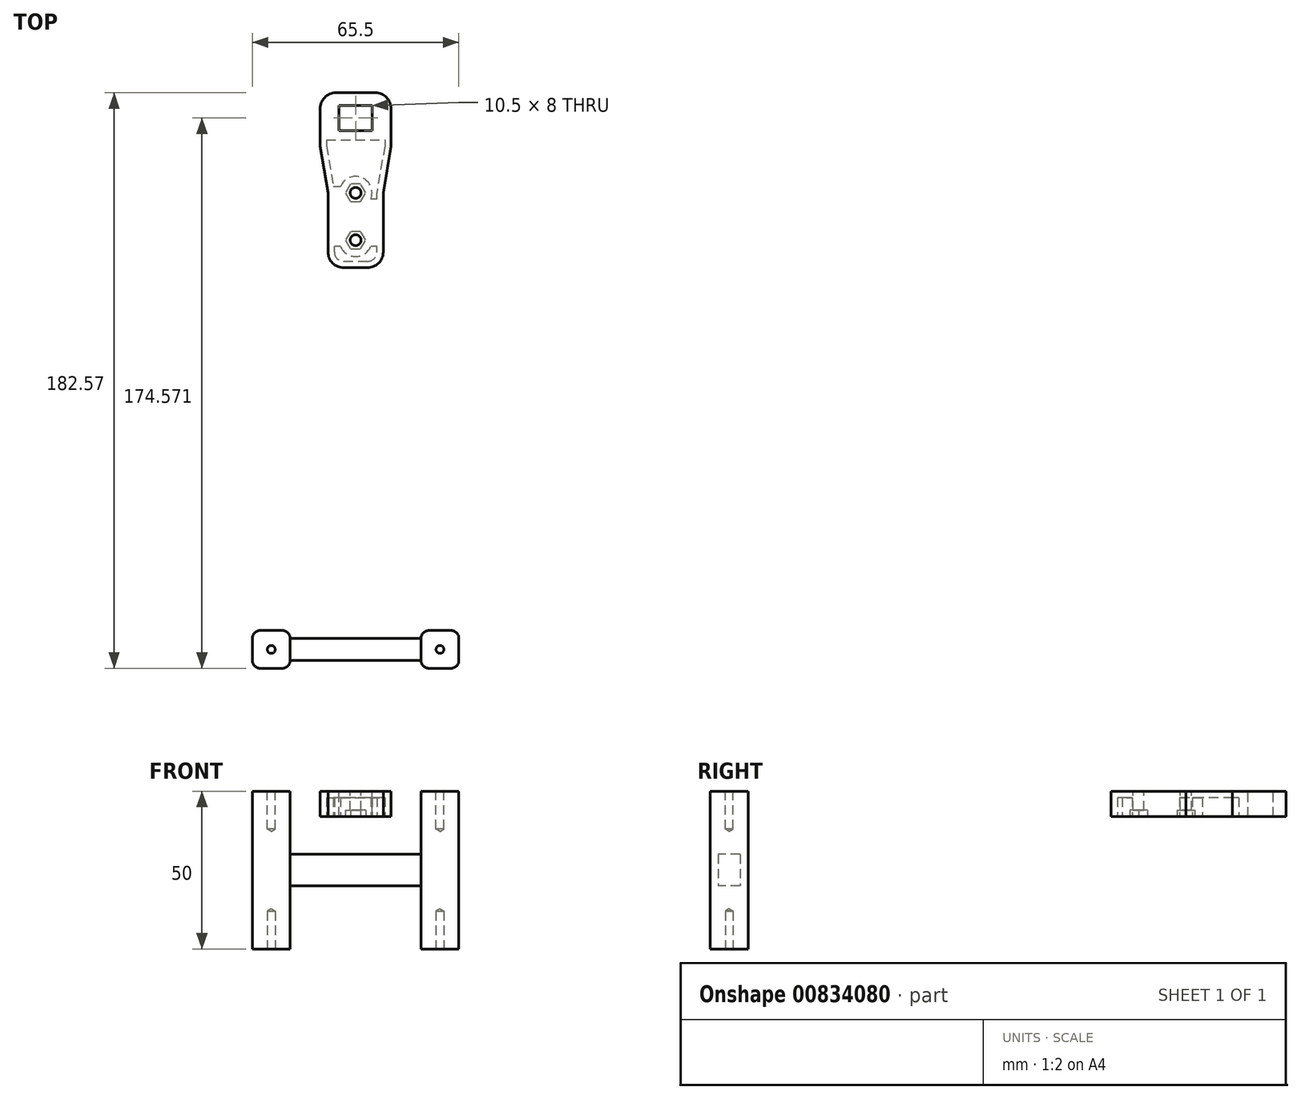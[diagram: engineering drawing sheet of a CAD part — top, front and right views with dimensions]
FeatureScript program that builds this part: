
annotation { "Feature Type Name" : "Feature", "Feature Type Description" : "" }
export const myFeature = defineFeature(function(context is Context, id is Id, definition is map)
    precondition{}
    {
        {
            var Q0;
            Q0=qCreatedBy(makeId("Top.planeOp"),FACE);
            cPlane(context, id + "F0", {"entities" : qUnion([Q0]), "cplaneType" : CPlaneType.OFFSET, "offset" : 5 * mm, "oppositeDirection" : true, "width" : 150 * mm, "height" : 150 * mm});
        }
        {
            var Q0;
            Q0=qCreatedBy(makeId("Top.planeOp"),FACE);
            cPlane(context, id + "F1", {"entities" : qUnion([Q0]), "cplaneType" : CPlaneType.OFFSET, "offset" : 50 * mm, "oppositeDirection" : true, "width" : 150 * mm, "height" : 150 * mm});
        }
        {
            var Q0;
            Q0=qCreatedBy(id+"F1.planeOp",FACE);
            cPlane(context, id + "F2", {"entities" : qUnion([Q0]), "cplaneType" : CPlaneType.OFFSET, "offset" : 5 * mm, "width" : 150 * mm, "height" : 150 * mm});
        }
        {
            var Q0;
            Q0=qCreatedBy(id+"F0.planeOp",FACE);
            var sketch = newSketch(context, id + "F3", { "sketchPlane" : qUnion([Q0])});
            skLineSegment(sketch, "E0.bottom", {"start": v(28, -42.5) * mm, "end": v(-28, -42.5) * mm});
            skLineSegment(sketch, "E0.top", {"start": v(28, 42.5) * mm, "end": v(-28, 42.5) * mm});
            skLineSegment(sketch, "E0.left", {"start": v(28, -42.5) * mm, "end": v(28, 42.5) * mm});
            skLineSegment(sketch, "E0.right", {"start": v(-28, -42.5) * mm, "end": v(-28, 42.5) * mm});
            skPoint(sketch, "E0.middle", {"position": v(0, 0) * mm});
            skLineSegment(sketch, "E1", {"start": v(0, 42.5) * mm, "end": v(0, -42.5) * mm, "construction": true});
            skLineSegment(sketch, "E2.bottom", {"start": v(-24.5, 19) * mm, "end": v(24.5, 19) * mm, "construction": true});
            skLineSegment(sketch, "E2.top", {"start": v(-24.5, -39) * mm, "end": v(24.5, -39) * mm, "construction": true});
            skLineSegment(sketch, "E2.left", {"start": v(-24.5, 19) * mm, "end": v(-24.5, -39) * mm, "construction": true});
            skLineSegment(sketch, "E2.right", {"start": v(24.5, 19) * mm, "end": v(24.5, -39) * mm, "construction": true});
            skPoint(sketch, "E3", {"position": v(0, -39) * mm});
            skCircle(sketch, "E4", {"center": v(-24.5, 19) * mm, "radius": 1.38 * mm});
            skCircle(sketch, "E5", {"center": v(24.5, 19) * mm, "radius": 1.38 * mm});
            skCircle(sketch, "E6", {"center": v(-24.5, -39) * mm, "radius": 1.38 * mm});
            skCircle(sketch, "E7", {"center": v(24.5, -39) * mm, "radius": 1.38 * mm});
            skSolve(sketch);
        }
        {
            var Q0;
            Q0=qCreatedBy(id+"F2.planeOp",FACE);
            var sketch = newSketch(context, id + "F4", { "sketchPlane" : qUnion([Q0])});
            skLineSegment(sketch, "E8.bottom", {"start": v(26.65, -50.8) * mm, "end": v(-26.65, -50.8) * mm});
            skLineSegment(sketch, "E8.top", {"start": v(26.65, 50.8) * mm, "end": v(-26.65, 50.8) * mm});
            skLineSegment(sketch, "E8.left", {"start": v(26.65, -50.8) * mm, "end": v(26.65, 50.8) * mm});
            skLineSegment(sketch, "E8.right", {"start": v(-26.65, -50.8) * mm, "end": v(-26.65, 50.8) * mm});
            skPoint(sketch, "E8.middle", {"position": v(0, 0) * mm});
            skLineSegment(sketch, "E9", {"start": v(-24.15, 36.8) * mm, "end": v(-24.15, -45.4) * mm, "construction": true});
            skCircle(sketch, "E10", {"center": v(-24.15, 36.8) * mm, "radius": 1.75 * mm});
            skLineSegment(sketch, "E11", {"start": v(24.05, 35.5) * mm, "end": v(24.05, -39.4) * mm, "construction": true});
            skLineSegment(sketch, "E12", {"start": v(-19.05, -15.3) * mm, "end": v(8.85, -15.3) * mm, "construction": true});
            skCircle(sketch, "E13", {"center": v(-24.15, -45.4) * mm, "radius": 1.75 * mm});
            skCircle(sketch, "E14", {"center": v(-19.05, -15.3) * mm, "radius": 1.75 * mm});
            skCircle(sketch, "E15", {"center": v(8.85, -15.3) * mm, "radius": 1.75 * mm});
            skCircle(sketch, "E16", {"center": v(24.05, -39.4) * mm, "radius": 1.75 * mm});
            skCircle(sketch, "E17", {"center": v(24.05, 35.5) * mm, "radius": 1.75 * mm});
            skSolve(sketch);
        }
        {
            var Q0;
            Q0=qCreatedBy(makeId("Top.planeOp"),FACE);
            var sketch = newSketch(context, id + "F5", { "sketchPlane" : qUnion([Q0])});
            skPoint(sketch, "E18", {"position": v(-78, 0) * mm});
            skLineSegment(sketch, "E19", {"start": v(-78, 0) * mm, "end": v(0, 0) * mm, "construction": true});
            skPoint(sketch, "E20", {"position": v(-35, 0) * mm});
            skArc(sketch, "E21", {"start": v(-41.72, 93.39) * mm, "mid": v(-69.28, 91.47) * mm, "end": v(-68.64, 63.86) * mm});
            skArc(sketch, "E22", {"start": v(-81.47, 19.7) * mm, "mid": v(-98, 0) * mm, "end": v(-81.47, -19.7) * mm});
            skLineSegment(sketch, "E23", {"start": v(-54.5, 78) * mm, "end": v(0, 78) * mm, "construction": true});
            skLineSegment(sketch, "E24", {"start": v(0, 78) * mm, "end": v(0, 0) * mm, "construction": true});
            skArc(sketch, "E25.MirrorC", {"start": v(-41.72, -93.39) * mm, "mid": v(-69.28, -91.47) * mm, "end": v(-68.64, -63.86) * mm});
            skArc(sketch, "E26.MirrorC", {"start": v(41.72, 93.39) * mm, "mid": v(69.28, 91.47) * mm, "end": v(68.64, 63.86) * mm});
            skArc(sketch, "E27.MirrorC", {"start": v(81.47, 19.7) * mm, "mid": v(98, 0) * mm, "end": v(81.47, -19.7) * mm});
            skArc(sketch, "E28.MirrorC", {"start": v(41.72, -93.39) * mm, "mid": v(69.28, -91.47) * mm, "end": v(68.64, -63.86) * mm});
            skLineSegment(sketch, "E29", {"start": v(-54.5, 78) * mm, "end": v(-84.27, 48.23) * mm, "construction": true});
            skLineSegment(sketch, "E30", {"start": v(-78, 0) * mm, "end": v(-85.72, 43.8) * mm, "construction": true});
            skArc(sketch, "E31", {"start": v(-81.47, 19.7) * mm, "mid": v(-62.72, 38.2) * mm, "end": v(-68.64, 63.86) * mm});
            skArc(sketch, "E32.MirrorCS", {"start": v(-81.47, -19.7) * mm, "mid": v(-62.72, -38.2) * mm, "end": v(-68.64, -63.86) * mm});
            skArc(sketch, "E33.MirrorCS", {"start": v(81.47, 19.7) * mm, "mid": v(62.72, 38.2) * mm, "end": v(68.64, 63.86) * mm});
            skArc(sketch, "E34.MirrorCS", {"start": v(81.47, -19.7) * mm, "mid": v(62.72, -38.2) * mm, "end": v(68.64, -63.86) * mm});
            skPoint(sketch, "E35", {"position": v(0, 143.63) * mm});
            skLineSegment(sketch, "E36", {"start": v(54.5, 78) * mm, "end": v(0, 143.63) * mm, "construction": true});
            skArc(sketch, "E37", {"start": v(41.72, 93.39) * mm, "mid": v(0, 78.32) * mm, "end": v(-41.72, 93.39) * mm});
            skArc(sketch, "E38.MirrorCS", {"start": v(41.72, -93.39) * mm, "mid": v(0, -78.32) * mm, "end": v(-41.72, -93.39) * mm});
            skLineSegment(sketch, "E39", {"start": v(-65, 78) * mm, "end": v(-44, 78) * mm, "construction": true});
            skLineSegment(sketch, "E40", {"start": v(-54.5, 88.5) * mm, "end": v(-54.5, 67.5) * mm, "construction": true});
            skCircle(sketch, "E41", {"center": v(-54.5, 88.5) * mm, "radius": 1.25 * mm});
            skCircle(sketch, "E42", {"center": v(-44, 78) * mm, "radius": 1.25 * mm});
            skCircle(sketch, "E43", {"center": v(-54.5, 67.5) * mm, "radius": 1.25 * mm});
            skCircle(sketch, "E44", {"center": v(-65, 78) * mm, "radius": 1.25 * mm});
            skCircle(sketch, "E45", {"center": v(-54.5, 78) * mm, "radius": 4.5 * mm});
            skCircle(sketch, "E46.MirrorC", {"center": v(-54.5, -88.5) * mm, "radius": 1.25 * mm});
            skCircle(sketch, "E47.MirrorC", {"center": v(-44, -78) * mm, "radius": 1.25 * mm});
            skCircle(sketch, "E48.MirrorC", {"center": v(-54.5, -67.5) * mm, "radius": 1.25 * mm});
            skCircle(sketch, "E49.MirrorC", {"center": v(-65, -78) * mm, "radius": 1.25 * mm});
            skCircle(sketch, "E50.MirrorC", {"center": v(-54.5, -78) * mm, "radius": 4.5 * mm});
            skCircle(sketch, "E51.MirrorC", {"center": v(54.5, 88.5) * mm, "radius": 1.25 * mm});
            skCircle(sketch, "E52.MirrorC", {"center": v(44, 78) * mm, "radius": 1.25 * mm});
            skCircle(sketch, "E53.MirrorC", {"center": v(54.5, 67.5) * mm, "radius": 1.25 * mm});
            skCircle(sketch, "E54.MirrorC", {"center": v(65, 78) * mm, "radius": 1.25 * mm});
            skCircle(sketch, "E55.MirrorC", {"center": v(54.5, 78) * mm, "radius": 4.5 * mm});
            skCircle(sketch, "E56.MirrorC", {"center": v(54.5, -67.5) * mm, "radius": 1.25 * mm});
            skCircle(sketch, "E57.MirrorC", {"center": v(44, -78) * mm, "radius": 1.25 * mm});
            skCircle(sketch, "E58.MirrorC", {"center": v(54.5, -88.5) * mm, "radius": 1.25 * mm});
            skCircle(sketch, "E59.MirrorC", {"center": v(65, -78) * mm, "radius": 1.25 * mm});
            skCircle(sketch, "E60.MirrorC", {"center": v(54.5, -78) * mm, "radius": 4.5 * mm});
            skLineSegment(sketch, "E61", {"start": v(-88.5, 0) * mm, "end": v(-67.5, 0) * mm, "construction": true});
            skLineSegment(sketch, "E62", {"start": v(-78, 10.5) * mm, "end": v(-78, -10.5) * mm, "construction": true});
            skCircle(sketch, "E63", {"center": v(-78, 10.5) * mm, "radius": 1.25 * mm});
            skCircle(sketch, "E64", {"center": v(-67.5, 0) * mm, "radius": 1.25 * mm});
            skCircle(sketch, "E65", {"center": v(-78, -10.5) * mm, "radius": 1.25 * mm});
            skCircle(sketch, "E66", {"center": v(-88.5, 0) * mm, "radius": 1.25 * mm});
            skCircle(sketch, "E67", {"center": v(-78, 0) * mm, "radius": 4.5 * mm});
            skCircle(sketch, "E68.MirrorC", {"center": v(78, 0) * mm, "radius": 4.5 * mm});
            skCircle(sketch, "E69.MirrorC", {"center": v(67.5, 0) * mm, "radius": 1.25 * mm});
            skCircle(sketch, "E70.MirrorC", {"center": v(78, 10.5) * mm, "radius": 1.25 * mm});
            skCircle(sketch, "E71.MirrorC", {"center": v(88.5, 0) * mm, "radius": 1.25 * mm});
            skCircle(sketch, "E72.MirrorC", {"center": v(78, -10.5) * mm, "radius": 1.25 * mm});
            skCircle(sketch, "E73", {"center": v(-26.75, 74.5) * mm, "radius": 1.75 * mm});
            skCircle(sketch, "E74.MirrorC", {"center": v(26.75, 74.5) * mm, "radius": 1.75 * mm});
            skCircle(sketch, "E75.MirrorC", {"center": v(-26.75, -74.5) * mm, "radius": 1.75 * mm});
            skCircle(sketch, "E76.MirrorC", {"center": v(26.75, -74.5) * mm, "radius": 1.75 * mm});
            skCircle(sketch, "E77", {"center": v(0, 70.32) * mm, "radius": 1.75 * mm});
            skCircle(sketch, "E78", {"center": v(0, 55.32) * mm, "radius": 1.75 * mm});
            skLineSegment(sketch, "E79.bottom", {"start": v(-21, 12.5) * mm, "end": v(-17, 12.5) * mm});
            skLineSegment(sketch, "E79.top", {"start": v(-21, -12.5) * mm, "end": v(-17, -12.5) * mm});
            skLineSegment(sketch, "E79.left", {"start": v(-21, 12.5) * mm, "end": v(-21, -12.5) * mm});
            skLineSegment(sketch, "E79.right", {"start": v(-17, 12.5) * mm, "end": v(-17, -12.5) * mm});
            skPoint(sketch, "E80", {"position": v(-17, 0) * mm});
            skLineSegment(sketch, "E81.MirrorCS", {"start": v(17, 12.5) * mm, "end": v(17, -12.5) * mm});
            skLineSegment(sketch, "E82.MirrorCS", {"start": v(21, 12.5) * mm, "end": v(21, -12.5) * mm});
            skLineSegment(sketch, "E83.MirrorCS", {"start": v(21, -12.5) * mm, "end": v(17, -12.5) * mm});
            skLineSegment(sketch, "E84.MirrorCS", {"start": v(21, 12.5) * mm, "end": v(17, 12.5) * mm});
            skCircle(sketch, "E85.0", {"center": v(24.5, 19) * mm, "radius": 1.38 * mm});
            skCircle(sketch, "E86.0", {"center": v(24.5, -39) * mm, "radius": 1.38 * mm});
            skCircle(sketch, "E87.0", {"center": v(-24.5, -39) * mm, "radius": 1.38 * mm});
            skCircle(sketch, "E88.0", {"center": v(-24.5, 19) * mm, "radius": 1.38 * mm});
            skLineSegment(sketch, "E89", {"start": v(-26.75, -74.5) * mm, "end": v(26.75, -74.5) * mm, "construction": true});
            skSolve(sketch);
        }
        {
            var Q0;
            Q0=qCreatedBy(id+"F1.planeOp",FACE);
            var sketch = newSketch(context, id + "F6", { "sketchPlane" : qUnion([Q0])});
            skArc(sketch, "E90.0", {"start": v(41.72, 93.39) * mm, "mid": v(0, 78.32) * mm, "end": v(-41.72, 93.39) * mm});
            skArc(sketch, "E91.0", {"start": v(-41.72, 93.39) * mm, "mid": v(-69.28, 91.47) * mm, "end": v(-68.64, 63.86) * mm});
            skArc(sketch, "E92.0", {"start": v(-81.47, 19.7) * mm, "mid": v(-62.72, 38.2) * mm, "end": v(-68.64, 63.86) * mm});
            skArc(sketch, "E93.0", {"start": v(-81.47, 19.7) * mm, "mid": v(-98, 0) * mm, "end": v(-81.47, -19.7) * mm});
            skArc(sketch, "E94.0", {"start": v(-81.47, -19.7) * mm, "mid": v(-62.72, -38.2) * mm, "end": v(-68.64, -63.86) * mm});
            skArc(sketch, "E95.0", {"start": v(-41.72, -93.39) * mm, "mid": v(-69.28, -91.47) * mm, "end": v(-68.64, -63.86) * mm});
            skArc(sketch, "E96.0", {"start": v(41.72, -93.39) * mm, "mid": v(0, -78.32) * mm, "end": v(-41.72, -93.39) * mm});
            skArc(sketch, "E97.0", {"start": v(41.72, -93.39) * mm, "mid": v(69.28, -91.47) * mm, "end": v(68.64, -63.86) * mm});
            skArc(sketch, "E98.0", {"start": v(81.47, -19.7) * mm, "mid": v(62.72, -38.2) * mm, "end": v(68.64, -63.86) * mm});
            skArc(sketch, "E99.0", {"start": v(81.47, 19.7) * mm, "mid": v(98, 0) * mm, "end": v(81.47, -19.7) * mm});
            skArc(sketch, "E100.0", {"start": v(81.47, 19.7) * mm, "mid": v(62.72, 38.2) * mm, "end": v(68.64, 63.86) * mm});
            skArc(sketch, "E101.0", {"start": v(41.72, 93.39) * mm, "mid": v(69.28, 91.47) * mm, "end": v(68.64, 63.86) * mm});
            skCircle(sketch, "E102.0", {"center": v(26.75, 74.5) * mm, "radius": 1.75 * mm});
            skCircle(sketch, "E103.0", {"center": v(-26.75, 74.5) * mm, "radius": 1.75 * mm});
            skCircle(sketch, "E104.0", {"center": v(26.75, -74.5) * mm, "radius": 1.75 * mm});
            skCircle(sketch, "E105.0", {"center": v(-26.75, -74.5) * mm, "radius": 1.75 * mm});
            skCircle(sketch, "E106", {"center": v(-78, 0) * mm, "radius": 2.25 * mm});
            skCircle(sketch, "E107", {"center": v(-54.5, 78) * mm, "radius": 2.25 * mm});
            skLineSegment(sketch, "E108.0", {"start": v(0, 78) * mm, "end": v(0, 0) * mm, "construction": true});
            skLineSegment(sketch, "E109.0", {"start": v(-78, 0) * mm, "end": v(0, 0) * mm, "construction": true});
            skCircle(sketch, "E110.MirrorC", {"center": v(-54.5, -78) * mm, "radius": 2.25 * mm});
            skCircle(sketch, "E111.MirrorC", {"center": v(54.5, 78) * mm, "radius": 2.25 * mm});
            skCircle(sketch, "E112.MirrorC", {"center": v(78, 0) * mm, "radius": 2.25 * mm});
            skCircle(sketch, "E113.MirrorC", {"center": v(54.5, -78) * mm, "radius": 2.25 * mm});
            skCircle(sketch, "E114.0", {"center": v(-24.15, 36.8) * mm, "radius": 1.75 * mm});
            skCircle(sketch, "E115.0", {"center": v(-19.05, -15.3) * mm, "radius": 1.75 * mm});
            skCircle(sketch, "E116.0", {"center": v(-24.15, -45.4) * mm, "radius": 1.75 * mm});
            skCircle(sketch, "E117.0", {"center": v(24.05, -39.4) * mm, "radius": 1.75 * mm});
            skCircle(sketch, "E118.0", {"center": v(8.85, -15.3) * mm, "radius": 1.75 * mm});
            skCircle(sketch, "E119.0", {"center": v(24.05, 35.5) * mm, "radius": 1.75 * mm});
            skSolve(sketch);
        }
        {
            var Q0;
            Q0=qCreatedBy(makeId("Top.planeOp"),FACE);
            var sketch = newSketch(context, id + "F7", { "sketchPlane" : qUnion([Q0])});
            skCircle(sketch, "E120.0", {"center": v(0, 70.32) * mm, "radius": 1.75 * mm});
            skCircle(sketch, "E121.0", {"center": v(0, 55.32) * mm, "radius": 1.75 * mm});
            skLineSegment(sketch, "E122", {"start": v(0, 0) * mm, "end": v(0, 115.27) * mm, "construction": true});
            skLineSegment(sketch, "E123.bottom", {"start": v(8.75, 46.57) * mm, "end": v(-8.75, 46.57) * mm});
            skLineSegment(sketch, "E123.top", {"start": v(8.75, 102.07) * mm, "end": v(-8.75, 102.07) * mm});
            skLineSegment(sketch, "E123.left", {"start": v(8.75, 46.57) * mm, "end": v(8.75, 102.07) * mm});
            skLineSegment(sketch, "E123.right", {"start": v(-8.75, 46.57) * mm, "end": v(-8.75, 102.07) * mm});
            skPoint(sketch, "E123.middle", {"position": v(0, 74.32) * mm});
            skLineSegment(sketch, "E124.bottom", {"start": v(5.25, 90.07) * mm, "end": v(-5.25, 90.07) * mm});
            skLineSegment(sketch, "E124.top", {"start": v(5.25, 98.07) * mm, "end": v(-5.25, 98.07) * mm});
            skLineSegment(sketch, "E124.left", {"start": v(5.25, 90.07) * mm, "end": v(5.25, 98.07) * mm});
            skLineSegment(sketch, "E124.right", {"start": v(-5.25, 90.07) * mm, "end": v(-5.25, 98.07) * mm});
            skPoint(sketch, "E124.middle", {"position": v(0, 94.07) * mm});
            skLineSegment(sketch, "E125.bottom", {"start": v(-11.25, 102.07) * mm, "end": v(11.25, 102.07) * mm});
            skLineSegment(sketch, "E125.top", {"start": v(-11.25, 85.07) * mm, "end": v(11.25, 85.07) * mm});
            skLineSegment(sketch, "E125.left", {"start": v(-11.25, 102.07) * mm, "end": v(-11.25, 85.07) * mm});
            skLineSegment(sketch, "E125.right", {"start": v(11.25, 102.07) * mm, "end": v(11.25, 85.07) * mm});
            skPoint(sketch, "E125.middle", {"position": v(0, 93.57) * mm});
            skLineSegment(sketch, "E126", {"start": v(11.25, 85.07) * mm, "end": v(8.75, 70.32) * mm});
            skLineSegment(sketch, "E127", {"start": v(-11.25, 85.07) * mm, "end": v(-8.75, 70.32) * mm});
            skSolve(sketch);
        }
        {
            var Q0;
            {var subQ5=sQuery(id+"F7.wireOp",EDGE,"E125.right");Q0=makeQuery(id+"F7.imprint","IMPRINT",FACE,{"disambiguationData":[TD([[makeQuery(id+"F7.imprint","IMPRINT",EDGE,{"derivedFrom":subQ5}),-1.0]])]});}
            var Q1;
            Q1=makeQuery(id+"F7.imprint","IMPRINT",FACE,{"disambiguationData":[TD([[makeQuery(id+"F7.imprint","IMPRINT",EDGE,{"derivedFrom":sQuery(id+"F7.wireOp",EDGE,"E124.bottom")}),1.0]])]});
            var Q2;
            {var subQ5=sQuery(id+"F7.wireOp",EDGE,"E125.left");Q2=makeQuery(id+"F7.imprint","IMPRINT",FACE,{"disambiguationData":[TD([[makeQuery(id+"F7.imprint","IMPRINT",EDGE,{"derivedFrom":subQ5}),1.0]])]});}
            var Q3;
            {var subQ0=sQuery(id+"F7.wireOp",EDGE,"E127");Q3=makeQuery(id+"F7.imprint","IMPRINT",FACE,{"disambiguationData":[TD([[makeQuery(id+"F7.imprint","IMPRINT",EDGE,{"derivedFrom":subQ0}),1.0]])]});}
            var Q4;
            Q4=makeQuery(id+"F7.imprint","IMPRINT",FACE,{"disambiguationData":[TD([[makeQuery(id+"F7.imprint","IMPRINT",EDGE,{"derivedFrom":sQuery(id+"F7.wireOp",EDGE,"E120.0")}),-1.0]])]});
            var Q5;
            {var subQ0=sQuery(id+"F7.wireOp",EDGE,"E126");Q5=makeQuery(id+"F7.imprint","IMPRINT",FACE,{"disambiguationData":[TD([[makeQuery(id+"F7.imprint","IMPRINT",EDGE,{"derivedFrom":subQ0}),-1.0]])]});}
            extrude(context, id + "F8", {"entities" : qUnion([Q0, Q1, Q2, Q3, Q4, Q5]), "oppositeDirection" : true, "depth" : 8 * mm});
        }
        {
            var Q0;
            Q0=makeQuery(id+"F8.opExtrude","SWEPT_EDGE",EDGE,{"disambiguationData":[OSD([sQuery(id+"F7.wireOp",EDGE,"E125.bottom"),sQuery(id+"F7.wireOp",EDGE,"E125.right")])]});
            var Q1;
            Q1=makeQuery(id+"F8.opExtrude","SWEPT_EDGE",EDGE,{"disambiguationData":[OSD([sQuery(id+"F7.wireOp",EDGE,"E123.bottom"),sQuery(id+"F7.wireOp",EDGE,"E123.left")])]});
            var Q2;
            Q2=makeQuery(id+"F8.opExtrude","SWEPT_EDGE",EDGE,{"disambiguationData":[OSD([sQuery(id+"F7.wireOp",EDGE,"E123.bottom"),sQuery(id+"F7.wireOp",EDGE,"E123.right")])]});
            var Q3;
            Q3=makeQuery(id+"F8.opExtrude","SWEPT_EDGE",EDGE,{"disambiguationData":[OSD([sQuery(id+"F7.wireOp",EDGE,"E125.bottom"),sQuery(id+"F7.wireOp",EDGE,"E125.left")])]});
            fillet(context, id + "F9", {"entities" : qUnion([Q0, Q1, Q2, Q3]), "radius" : 5 * mm, "tangentPropagation" : true, "allowEdgeOverflow" : false});
        }
        {
            var Q0;
            Q0=makeQuery(id+"F8.opExtrude","CAP_FACE",FACE,{"disambiguationData":[OSD([sQuery(id+"F7.wireOp",EDGE,"E120.0"),sQuery(id+"F7.wireOp",EDGE,"E121.0"),sQuery(id+"F7.wireOp",EDGE,"E123.bottom"),sQuery(id+"F7.wireOp",EDGE,"E123.left"),sQuery(id+"F7.wireOp",EDGE,"E123.right"),sQuery(id+"F7.wireOp",EDGE,"E124.bottom"),sQuery(id+"F7.wireOp",EDGE,"E124.top"),sQuery(id+"F7.wireOp",EDGE,"E124.left"),sQuery(id+"F7.wireOp",EDGE,"E124.right"),sQuery(id+"F7.wireOp",EDGE,"E125.bottom"),sQuery(id+"F7.wireOp",EDGE,"E125.left"),sQuery(id+"F7.wireOp",EDGE,"E125.right"),sQuery(id+"F7.wireOp",EDGE,"E126"),sQuery(id+"F7.wireOp",EDGE,"E127")])],"isStart":false});
            var sketch = newSketch(context, id + "F10", { "sketchPlane" : qUnion([Q0])});
            skCircle(sketch, "E128.cCircle", {"center": v(0, -55.32) * mm, "radius": 2.77 * mm, "construction": true});
            skLineSegment(sketch, "E128.0", {"start": v(1.6, -58.1) * mm, "end": v(-1.6, -58.1) * mm});
            skLineSegment(sketch, "E128.1", {"start": v(-1.6, -58.1) * mm, "end": v(-3.2, -55.32) * mm});
            skLineSegment(sketch, "E128.2", {"start": v(-3.2, -55.32) * mm, "end": v(-1.6, -52.55) * mm});
            skLineSegment(sketch, "E128.3", {"start": v(-1.6, -52.55) * mm, "end": v(1.6, -52.55) * mm});
            skLineSegment(sketch, "E128.4", {"start": v(1.6, -52.55) * mm, "end": v(3.2, -55.32) * mm});
            skLineSegment(sketch, "E128.5", {"start": v(3.2, -55.32) * mm, "end": v(1.6, -58.1) * mm});
            skPoint(sketch, "E128.0.midPoint", {"position": v(0, -58.1) * mm});
            skCircle(sketch, "E129.cCircle", {"center": v(0, -70.32) * mm, "radius": 2.77 * mm, "construction": true});
            skLineSegment(sketch, "E129.0", {"start": v(-1.6, -67.55) * mm, "end": v(1.6, -67.55) * mm});
            skLineSegment(sketch, "E129.1", {"start": v(1.6, -67.55) * mm, "end": v(3.2, -70.32) * mm});
            skLineSegment(sketch, "E129.2", {"start": v(3.2, -70.32) * mm, "end": v(1.6, -73.1) * mm});
            skLineSegment(sketch, "E129.3", {"start": v(1.6, -73.1) * mm, "end": v(-1.6, -73.1) * mm});
            skLineSegment(sketch, "E129.4", {"start": v(-1.6, -73.1) * mm, "end": v(-3.2, -70.32) * mm});
            skLineSegment(sketch, "E129.5", {"start": v(-3.2, -70.32) * mm, "end": v(-1.6, -67.55) * mm});
            skPoint(sketch, "E129.0.midPoint", {"position": v(0, -67.55) * mm});
            skLineSegment(sketch, "E130.0", {"start": v(-9.25, -87.07) * mm, "end": v(-9.25, -85.24) * mm});
            skLineSegment(sketch, "E130.1", {"start": v(-9.25, -85.24) * mm, "end": v(-6.75, -70.49) * mm});
            skLineSegment(sketch, "E130.2", {"start": v(-6.75, -51.57) * mm, "end": v(-6.75, -70.49) * mm});
            skArc(sketch, "E130.3", {"start": v(-3.75, -48.57) * mm, "mid": v(-5.87, -49.45) * mm, "end": v(-6.75, -51.57) * mm});
            skLineSegment(sketch, "E130.4", {"start": v(3.75, -48.57) * mm, "end": v(-3.75, -48.57) * mm});
            skLineSegment(sketch, "E130.5", {"start": v(9.25, -87.07) * mm, "end": v(9.25, -85.24) * mm});
            skLineSegment(sketch, "E130.6", {"start": v(9.25, -85.24) * mm, "end": v(6.75, -70.49) * mm});
            skLineSegment(sketch, "E130.7", {"start": v(6.75, -51.57) * mm, "end": v(6.75, -70.49) * mm});
            skArc(sketch, "E130.8", {"start": v(6.75, -51.57) * mm, "mid": v(5.87, -49.45) * mm, "end": v(3.75, -48.57) * mm});
            skLineSegment(sketch, "E131", {"start": v(-9.25, -87.07) * mm, "end": v(9.25, -87.07) * mm});
            skCircle(sketch, "E132", {"center": v(0, -70.32) * mm, "radius": 5.2 * mm});
            skCircle(sketch, "E133", {"center": v(0, -55.32) * mm, "radius": 5.2 * mm});
            skLineSegment(sketch, "E134.bottom", {"start": v(6.75, -57.32) * mm, "end": v(-6.75, -57.32) * mm});
            skLineSegment(sketch, "E134.top", {"start": v(6.75, -53.32) * mm, "end": v(-6.75, -53.32) * mm});
            skLineSegment(sketch, "E134.left", {"start": v(6.75, -57.32) * mm, "end": v(6.75, -53.32) * mm});
            skLineSegment(sketch, "E134.right", {"start": v(-6.75, -57.32) * mm, "end": v(-6.75, -53.32) * mm});
            skLineSegment(sketch, "E135.bottom", {"start": v(7.06, -72.32) * mm, "end": v(-7.06, -72.32) * mm});
            skLineSegment(sketch, "E135.top", {"start": v(6.75, -68.32) * mm, "end": v(-6.75, -68.32) * mm});
            skPoint(sketch, "E135.right.end.orphan", {"position": v(-7.06, -68.32) * mm});
            skPoint(sketch, "E136.orphan", {"position": v(7.06, -68.32) * mm});
            skSolve(sketch);
        }
        {
            var Q0;
            {var subQ0=sQuery(id+"F10.wireOp",EDGE,"E135.top");var subQ1=sQuery(id+"F10.wireOp",EDGE,"E132");var subQ2=makeQuery(id+"F10.imprint","INTERSECT",VERTEX,{"disambiguationData":[OD(0.0)],"derivedFrom":[subQ1,subQ0]});Q0=makeQuery(id+"F10.imprint","IMPRINT",FACE,{"disambiguationData":[TD([[makeQuery(id+"F10.imprint","IMPRINT",EDGE,{"disambiguationData":[TD([[subQ2,1.0]])],"derivedFrom":subQ1}),-1.0]])]});}
            var Q1;
            {var subQ9=sQuery(id+"F10.wireOp",EDGE,"E130.3");Q1=makeQuery(id+"F10.imprint","IMPRINT",FACE,{"disambiguationData":[TD([[makeQuery(id+"F10.imprint","IMPRINT",EDGE,{"derivedFrom":subQ9}),1.0]])]});}
            var Q2;
            {var subQ5=sQuery(id+"F10.wireOp",EDGE,"E130.0");Q2=makeQuery(id+"F10.imprint","IMPRINT",FACE,{"disambiguationData":[TD([[makeQuery(id+"F10.imprint","IMPRINT",EDGE,{"derivedFrom":subQ5}),-1.0]])]});}
            extrude(context, id + "F11", {"entities" : qUnion([Q0, Q1, Q2]), "operationType" : NewBodyOperationType.REMOVE, "oppositeDirection" : true, "depth" : 6 * mm});
        }
        {
            var Q0;
            Q0=makeQuery(id+"F10.imprint","IMPRINT",FACE,{"disambiguationData":[TD([[makeQuery(id+"F10.imprint","IMPRINT",EDGE,{"derivedFrom":makeQuery(id+"F8.opExtrude","CAP_EDGE",EDGE,{"disambiguationData":[OSD([sQuery(id+"F7.wireOp",EDGE,"E121.0")])],"isStart":false})}),1.0]])]});
            var Q1;
            {var subQ0=sQuery(id+"F10.wireOp",EDGE,"E128.0");Q1=makeQuery(id+"F10.imprint","IMPRINT",FACE,{"disambiguationData":[TD([[makeQuery(id+"F10.imprint","IMPRINT",EDGE,{"derivedFrom":subQ0}),-1.0]])]});}
            var Q2;
            {var subQ0=sQuery(id+"F10.wireOp",EDGE,"E128.3");Q2=makeQuery(id+"F10.imprint","IMPRINT",FACE,{"disambiguationData":[TD([[makeQuery(id+"F10.imprint","IMPRINT",EDGE,{"derivedFrom":subQ0}),-1.0]])]});}
            var Q3;
            {var subQ0=sQuery(id+"F10.wireOp",EDGE,"E129.3");Q3=makeQuery(id+"F10.imprint","IMPRINT",FACE,{"disambiguationData":[TD([[makeQuery(id+"F10.imprint","IMPRINT",EDGE,{"derivedFrom":subQ0}),-1.0]])]});}
            var Q4;
            Q4=makeQuery(id+"F10.imprint","IMPRINT",FACE,{"disambiguationData":[TD([[makeQuery(id+"F10.imprint","IMPRINT",EDGE,{"derivedFrom":makeQuery(id+"F8.opExtrude","CAP_EDGE",EDGE,{"disambiguationData":[OSD([sQuery(id+"F7.wireOp",EDGE,"E120.0")])],"isStart":false})}),1.0]])]});
            var Q5;
            {var subQ0=sQuery(id+"F10.wireOp",EDGE,"E129.0");Q5=makeQuery(id+"F10.imprint","IMPRINT",FACE,{"disambiguationData":[TD([[makeQuery(id+"F10.imprint","IMPRINT",EDGE,{"derivedFrom":subQ0}),-1.0]])]});}
            extrude(context, id + "F12", {"entities" : qUnion([Q0, Q1, Q2, Q3, Q4, Q5]), "operationType" : NewBodyOperationType.REMOVE, "oppositeDirection" : true, "depth" : 2 * mm});
        }
        {
            var Q0;
            Q0=sQuery(id+"F5.wireOp",EDGE,"E89");
            cPlane(context, id + "F13", {"entities" : qUnion([Q0]), "cplaneType" : CPlaneType.LINE_ANGLE, "offset" : 25 * mm, "angle" : 0 * degree, "width" : 150 * mm, "height" : 150 * mm});
        }
        {
            var Q0;
            Q0=qCreatedBy(id+"F13.planeOp",FACE);
            var sketch = newSketch(context, id + "F14", { "sketchPlane" : qUnion([Q0])});
            skLineSegment(sketch, "E137.0", {"start": v(26.75, 0) * mm, "end": v(-26.75, 0) * mm, "construction": true});
            skLineSegment(sketch, "E138", {"start": v(0, 7.1) * mm, "end": v(0, -42.72) * mm, "construction": true});
            skLineSegment(sketch, "E139", {"start": v(0, -20) * mm, "end": v(20.75, -20) * mm});
            skLineSegment(sketch, "E140", {"start": v(20.75, -20) * mm, "end": v(20.75, 0) * mm});
            skLineSegment(sketch, "E141", {"start": v(20.75, 0) * mm, "end": v(32.75, 0) * mm});
            skLineSegment(sketch, "E142", {"start": v(32.75, 0) * mm, "end": v(32.75, -25) * mm});
            skLineSegment(sketch, "E143", {"start": v(48.37, -25) * mm, "end": v(-51.26, -25) * mm, "construction": true});
            skLineSegment(sketch, "E144.MirrorCS", {"start": v(0, -20) * mm, "end": v(-20.75, -20) * mm});
            skLineSegment(sketch, "E145.MirrorCS", {"start": v(-20.75, -20) * mm, "end": v(-20.75, 0) * mm});
            skLineSegment(sketch, "E146.MirrorCS", {"start": v(-20.75, 0) * mm, "end": v(-32.75, 0) * mm});
            skLineSegment(sketch, "E147.MirrorCS", {"start": v(-32.75, 0) * mm, "end": v(-32.75, -25) * mm});
            skLineSegment(sketch, "E148.MirrorCS", {"start": v(32.75, -50) * mm, "end": v(32.75, -25) * mm});
            skLineSegment(sketch, "E149.MirrorCS", {"start": v(20.75, -50) * mm, "end": v(32.75, -50) * mm});
            skLineSegment(sketch, "E150.MirrorCS", {"start": v(20.75, -30) * mm, "end": v(20.75, -50) * mm});
            skLineSegment(sketch, "E151.MirrorCS", {"start": v(0, -30) * mm, "end": v(20.75, -30) * mm});
            skLineSegment(sketch, "E152.MirrorCS", {"start": v(0, -30) * mm, "end": v(-20.75, -30) * mm});
            skLineSegment(sketch, "E153.MirrorCS", {"start": v(-20.75, -30) * mm, "end": v(-20.75, -50) * mm});
            skLineSegment(sketch, "E154.MirrorCS", {"start": v(-20.75, -50) * mm, "end": v(-32.75, -50) * mm});
            skLineSegment(sketch, "E155.MirrorCS", {"start": v(-32.75, -50) * mm, "end": v(-32.75, -25) * mm});
            skLineSegment(sketch, "E156", {"start": v(20.75, -20) * mm, "end": v(20.75, -30) * mm});
            skLineSegment(sketch, "E157", {"start": v(-20.75, -20) * mm, "end": v(-20.75, -30) * mm});
            skSolve(sketch);
        }
        {
            var Q0;
            Q0=makeQuery(id+"F14.imprint","IMPRINT",FACE,{"disambiguationData":[TD([[makeQuery(id+"F14.imprint","IMPRINT",EDGE,{"derivedFrom":sQuery(id+"F14.wireOp",EDGE,"E139")}),-1.0]])]});
            extrude(context, id + "F15", {"entities" : qUnion([Q0]), "endBound" : BoundingType.SYMMETRIC, "depth" : 7 * mm});
        }
        {
            var Q0;
            Q0=makeQuery(id+"F14.imprint","IMPRINT",FACE,{"disambiguationData":[TD([[makeQuery(id+"F14.imprint","IMPRINT",EDGE,{"derivedFrom":sQuery(id+"F14.wireOp",EDGE,"E140")}),-1.0]])]});
            var Q1;
            Q1=makeQuery(id+"F14.imprint","IMPRINT",FACE,{"disambiguationData":[TD([[makeQuery(id+"F14.imprint","IMPRINT",EDGE,{"derivedFrom":sQuery(id+"F14.wireOp",EDGE,"E145.MirrorCS")}),1.0]])]});
            extrude(context, id + "F16", {"entities" : qUnion([Q0, Q1]), "operationType" : NewBodyOperationType.ADD, "endBound" : BoundingType.SYMMETRIC, "depth" : 12 * mm});
        }
        {
            var Q0;
            Q0=makeQuery(id+"F16.opExtrude","SWEPT_FACE",FACE,{"disambiguationData":[OSD([sQuery(id+"F14.wireOp",EDGE,"E141")])]});
            var sketch = newSketch(context, id + "F17", { "sketchPlane" : qUnion([Q0])});
            skPoint(sketch, "E158.0", {"position": v(-26.75, -74.5) * mm});
            skPoint(sketch, "E159.0", {"position": v(26.75, -74.5) * mm});
            skSolve(sketch);
        }
        {
            var Q0;
            Q0=sQuery(id+"F17.wireOp",VERTEX,"E158.0");
            var Q1;
            Q1=sQuery(id+"F17.wireOp",VERTEX,"E159.0");
            var Q2;
            Q2=makeQuery(id+"F15.opExtrude","SWEPT_BODY",BODY,{"disambiguationData":[OSD([sQuery(id+"F14.wireOp",EDGE,"E139"),sQuery(id+"F14.wireOp",EDGE,"E144.MirrorCS"),sQuery(id+"F14.wireOp",EDGE,"E151.MirrorCS"),sQuery(id+"F14.wireOp",EDGE,"E152.MirrorCS"),sQuery(id+"F14.wireOp",EDGE,"E156"),sQuery(id+"F14.wireOp",EDGE,"E157")])]});
            hole(context, id + "F18", {"style" : HoleStyle.SIMPLE, "endStyle" : HoleEndStyle.BLIND, "holeDiameter" : 2.5 * mm, "holeDepth" : 12 * mm, "tappedDepth" : 12 * mm, "tapClearance" : 3, "locations" : qUnion([Q0, Q1]), "scope" : qUnion([Q2])});
        }
        {
            var Q0;
            Q0=makeQuery(id+"F16.opExtrude","SWEPT_FACE",FACE,{"disambiguationData":[OSD([sQuery(id+"F14.wireOp",EDGE,"E149.MirrorCS")])]});
            var sketch = newSketch(context, id + "F19", { "sketchPlane" : qUnion([Q0])});
            skPoint(sketch, "E160.0", {"position": v(-26.75, 74.5) * mm});
            skPoint(sketch, "E161.0", {"position": v(26.75, 74.5) * mm});
            skSolve(sketch);
        }
        {
            var Q0;
            Q0=sQuery(id+"F19.wireOp",VERTEX,"E160.0");
            var Q1;
            Q1=sQuery(id+"F19.wireOp",VERTEX,"E161.0");
            var Q2;
            Q2=makeQuery(id+"F15.opExtrude","SWEPT_BODY",BODY,{"disambiguationData":[OSD([sQuery(id+"F14.wireOp",EDGE,"E139"),sQuery(id+"F14.wireOp",EDGE,"E144.MirrorCS"),sQuery(id+"F14.wireOp",EDGE,"E151.MirrorCS"),sQuery(id+"F14.wireOp",EDGE,"E152.MirrorCS"),sQuery(id+"F14.wireOp",EDGE,"E156"),sQuery(id+"F14.wireOp",EDGE,"E157")])]});
            hole(context, id + "F20", {"style" : HoleStyle.SIMPLE, "endStyle" : HoleEndStyle.BLIND, "holeDiameter" : 2.5 * mm, "holeDepth" : 12 * mm, "tappedDepth" : 12 * mm, "tapClearance" : 3, "locations" : qUnion([Q0, Q1]), "scope" : qUnion([Q2])});
        }
        {
            var Q0;
            Q0=makeQuery(id+"F16.opExtrude","CAP_EDGE",EDGE,{"disambiguationData":[OSD([sQuery(id+"F14.wireOp",EDGE,"E140"),sQuery(id+"F14.wireOp",EDGE,"E150.MirrorCS"),sQuery(id+"F14.wireOp",EDGE,"E156")])],"isStart":true});
            var Q1;
            Q1=makeQuery(id+"F16.opExtrude","CAP_EDGE",EDGE,{"disambiguationData":[OSD([sQuery(id+"F14.wireOp",EDGE,"E140"),sQuery(id+"F14.wireOp",EDGE,"E150.MirrorCS"),sQuery(id+"F14.wireOp",EDGE,"E156")])],"isStart":false});
            var Q2;
            Q2=makeQuery(id+"F16.opExtrude","CAP_EDGE",EDGE,{"disambiguationData":[OSD([sQuery(id+"F14.wireOp",EDGE,"E142"),sQuery(id+"F14.wireOp",EDGE,"E148.MirrorCS")])],"isStart":true});
            var Q3;
            Q3=makeQuery(id+"F16.opExtrude","CAP_EDGE",EDGE,{"disambiguationData":[OSD([sQuery(id+"F14.wireOp",EDGE,"E145.MirrorCS"),sQuery(id+"F14.wireOp",EDGE,"E153.MirrorCS"),sQuery(id+"F14.wireOp",EDGE,"E157")])],"isStart":true});
            var Q4;
            Q4=makeQuery(id+"F16.opExtrude","CAP_EDGE",EDGE,{"disambiguationData":[OSD([sQuery(id+"F14.wireOp",EDGE,"E147.MirrorCS"),sQuery(id+"F14.wireOp",EDGE,"E155.MirrorCS")])],"isStart":true});
            var Q5;
            Q5=makeQuery(id+"F16.opExtrude","CAP_EDGE",EDGE,{"disambiguationData":[OSD([sQuery(id+"F14.wireOp",EDGE,"E147.MirrorCS"),sQuery(id+"F14.wireOp",EDGE,"E155.MirrorCS")])],"isStart":false});
            var Q6;
            Q6=makeQuery(id+"F16.opExtrude","CAP_EDGE",EDGE,{"disambiguationData":[OSD([sQuery(id+"F14.wireOp",EDGE,"E142"),sQuery(id+"F14.wireOp",EDGE,"E148.MirrorCS")])],"isStart":false});
            var Q7;
            Q7=makeQuery(id+"F16.opExtrude","CAP_EDGE",EDGE,{"disambiguationData":[OSD([sQuery(id+"F14.wireOp",EDGE,"E145.MirrorCS"),sQuery(id+"F14.wireOp",EDGE,"E153.MirrorCS"),sQuery(id+"F14.wireOp",EDGE,"E157")])],"isStart":false});
            fillet(context, id + "F21", {"entities" : qUnion([Q0, Q1, Q2, Q3, Q4, Q5, Q6, Q7]), "radius" : 2.5 * mm, "tangentPropagation" : true, "allowEdgeOverflow" : false});
        }
    });
